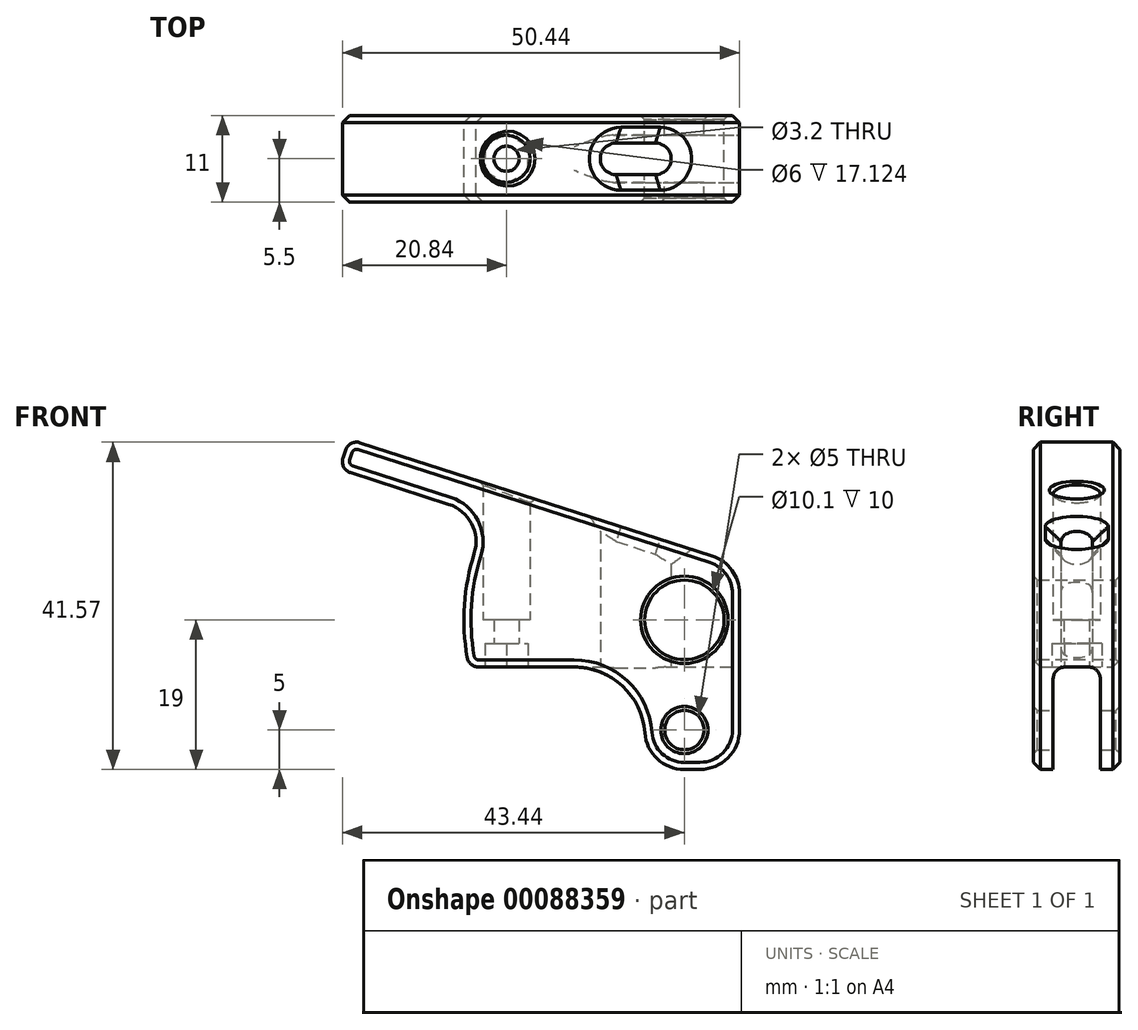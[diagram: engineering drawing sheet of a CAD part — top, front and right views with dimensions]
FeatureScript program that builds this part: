
annotation { "Feature Type Name" : "Feature", "Feature Type Description" : "" }
export const myFeature = defineFeature(function(context is Context, id is Id, definition is map)
    precondition{}
    {
        {
            var Q0;
            Q0=qCreatedBy(makeId("Front.planeOp"),FACE);
            var sketch = newSketch(context, id + "F0", { "sketchPlane" : qUnion([Q0])});
            skCircle(sketch, "E0", {"center": v(0, 0) * mm, "radius": 5.05 * mm});
            skCircle(sketch, "E1", {"center": v(0, -14) * mm, "radius": 2.5 * mm});
            skLineSegment(sketch, "E2.left", {"start": v(7, 7) * mm, "end": v(7, -19) * mm});
            skLineSegment(sketch, "E3.bottom", {"start": v(7, -19) * mm, "end": v(-5, -19) * mm});
            skLineSegment(sketch, "E3.right", {"start": v(-5, -19) * mm, "end": v(-5, -6) * mm});
            skLineSegment(sketch, "E4.trimOffspring", {"start": v(-5, -6) * mm, "end": v(-27.35, -6) * mm});
            skArc(sketch, "E5", {"start": v(-24.79, 13.02) * mm, "mid": v(-27.75, 3.74) * mm, "end": v(-27.35, -6) * mm});
            skLineSegment(sketch, "E6", {"start": v(-24.79, 13.02) * mm, "end": v(-43.83, 19.15) * mm});
            skLineSegment(sketch, "E7", {"start": v(-43.83, 19.15) * mm, "end": v(-42.6, 22.96) * mm});
            skLineSegment(sketch, "E8", {"start": v(-42.6, 22.96) * mm, "end": v(7, 7) * mm});
            skSolve(sketch);
        }
        {
            var Q0;
            Q0 = qSketchRegion(id + "F0", true);
            extrude(context, id + "F1", {"entities" : qUnion([Q0]), "endBound" : BoundingType.SYMMETRIC, "depth" : 11 * mm});
        }
        {
            var Q0;
            Q0=makeQuery(id+"F1.opExtrude","SWEPT_FACE",FACE,{"disambiguationData":[OSD([sQuery(id+"F0.wireOp",EDGE,"E3.bottom")])]});
            var sketch = newSketch(context, id + "F2", { "sketchPlane" : qUnion([Q0])});
            skLineSegment(sketch, "E9.bottom", {"start": v(7, 3) * mm, "end": v(-7, 3) * mm});
            skLineSegment(sketch, "E9.top", {"start": v(7, -3) * mm, "end": v(-7, -3) * mm});
            skLineSegment(sketch, "E9.left", {"start": v(7, 3) * mm, "end": v(7, -3) * mm});
            skLineSegment(sketch, "E9.right", {"start": v(-7, 3) * mm, "end": v(-7, -3) * mm});
            skPoint(sketch, "E9.middle", {"position": v(0, 0) * mm});
            skSolve(sketch);
        }
        {
            var Q0;
            Q0 = qSketchRegion(id + "F2", true);
            var Q1;
            Q1=makeQuery(id+"F1.opExtrude","SWEPT_FACE",FACE,{"disambiguationData":[OSD([sQuery(id+"F0.wireOp",EDGE,"E4.trimOffspring")])]});
            extrude(context, id + "F3", {"entities" : qUnion([Q0]), "operationType" : NewBodyOperationType.REMOVE, "endBound" : BoundingType.UP_TO_SURFACE, "oppositeDirection" : true, "endBoundEntityFace" : qUnion([Q1]), "depth" : 25 * mm});
        }
        {
            var Q0;
            Q0=makeQuery(id+"F3.boolean.opBoolean","MERGE",FACE,{"derivedFrom":[makeQuery(id+"F1.opExtrude","SWEPT_FACE",FACE,{"disambiguationData":[OSD([sQuery(id+"F0.wireOp",EDGE,"E4.trimOffspring")])]}),makeQuery(id+"F3.opExtrude","CAP_FACE",FACE,{"disambiguationData":[OSD([sQuery(id+"F2.wireOp",EDGE,"E9.bottom"),sQuery(id+"F2.wireOp",EDGE,"E9.top"),sQuery(id+"F2.wireOp",EDGE,"E9.left"),sQuery(id+"F2.wireOp",EDGE,"E9.right")])],"isStart":false})]});
            var sketch = newSketch(context, id + "F4", { "sketchPlane" : qUnion([Q0])});
            skLineSegment(sketch, "E10.bottom", {"start": v(-3.68, -2) * mm, "end": v(-8.68, -2) * mm});
            skLineSegment(sketch, "E10.top", {"start": v(-3.68, 2) * mm, "end": v(-8.68, 2) * mm});
            skPoint(sketch, "E10.middle", {"position": v(-6.18, 0) * mm});
            skArc(sketch, "E11", {"start": v(-8.68, 2) * mm, "mid": v(-10.68, 0) * mm, "end": v(-8.68, -2) * mm});
            skArc(sketch, "E12", {"start": v(-3.68, -2) * mm, "mid": v(-1.68, 0) * mm, "end": v(-3.68, 2) * mm});
            skSolve(sketch);
        }
        {
            var Q0;
            Q0 = qSketchRegion(id + "F4", true);
            extrude(context, id + "F5", {"entities" : qUnion([Q0]), "operationType" : NewBodyOperationType.REMOVE, "endBound" : BoundingType.THROUGH_ALL, "oppositeDirection" : true, "depth" : 25 * mm});
        }
        {
            var Q0;
            {var subQ0=sQuery(id+"F0.wireOp",EDGE,"E4.trimOffspring");var subQ2=sQuery(id+"F2.wireOp",EDGE,"E9.bottom");var subQ3=sQuery(id+"F0.wireOp",EDGE,"E3.right");Q0=makeQuery(id+"F3.boolean.opBoolean","SPLIT",EDGE,{"disambiguationData":[TD([makeQuery(id+"F3.opExtrude","SWEPT_FACE",FACE,{"disambiguationData":[OSD([subQ2])]})])],"derivedFrom":makeQuery(id+"F1.opExtrude","SWEPT_EDGE",EDGE,{"disambiguationData":[OSD([subQ3,subQ0])]})});}
            var Q1;
            {var subQ0=sQuery(id+"F0.wireOp",EDGE,"E4.trimOffspring");var subQ1=sQuery(id+"F0.wireOp",EDGE,"E3.right");var subQ3=sQuery(id+"F2.wireOp",EDGE,"E9.top");Q1=makeQuery(id+"F3.boolean.opBoolean","SPLIT",EDGE,{"disambiguationData":[TD([makeQuery(id+"F3.opExtrude","SWEPT_FACE",FACE,{"disambiguationData":[OSD([subQ3])]})])],"derivedFrom":makeQuery(id+"F1.opExtrude","SWEPT_EDGE",EDGE,{"disambiguationData":[OSD([subQ1,subQ0])]})});}
            fillet(context, id + "F6", {"entities" : qUnion([Q0, Q1]), "radius" : 9 * mm, "tangentPropagation" : true, "allowEdgeOverflow" : false});
        }
        {
            var Q0;
            {var subQ0=sQuery(id+"F0.wireOp",EDGE,"E3.right");var subQ1=sQuery(id+"F0.wireOp",EDGE,"E3.bottom");Q0=makeQuery(id+"F3.boolean.opBoolean","SPLIT",EDGE,{"disambiguationData":[TD([makeQuery(id+"F3.opExtrude","SWEPT_FACE",FACE,{"disambiguationData":[OSD([sQuery(id+"F2.wireOp",EDGE,"E9.bottom")])]})])],"derivedFrom":makeQuery(id+"F1.opExtrude","SWEPT_EDGE",EDGE,{"disambiguationData":[OSD([subQ1,subQ0])]})});}
            var Q1;
            {var subQ0=sQuery(id+"F0.wireOp",EDGE,"E3.right");var subQ1=sQuery(id+"F0.wireOp",EDGE,"E3.bottom");Q1=makeQuery(id+"F3.boolean.opBoolean","SPLIT",EDGE,{"disambiguationData":[TD([makeQuery(id+"F3.opExtrude","SWEPT_FACE",FACE,{"disambiguationData":[OSD([sQuery(id+"F2.wireOp",EDGE,"E9.top")])]})])],"derivedFrom":makeQuery(id+"F1.opExtrude","SWEPT_EDGE",EDGE,{"disambiguationData":[OSD([subQ1,subQ0])]})});}
            fillet(context, id + "F7", {"entities" : qUnion([Q0, Q1]), "radius" : 5 * mm, "tangentPropagation" : true, "allowEdgeOverflow" : false});
        }
        {
            var Q0;
            {var subQ0=sQuery(id+"F0.wireOp",EDGE,"E3.bottom");var subQ1=sQuery(id+"F0.wireOp",EDGE,"E2.left");Q0=makeQuery(id+"F3.boolean.opBoolean","SPLIT",EDGE,{"disambiguationData":[TD([makeQuery(id+"F3.opExtrude","SWEPT_FACE",FACE,{"disambiguationData":[OSD([sQuery(id+"F2.wireOp",EDGE,"E9.bottom")])]})])],"derivedFrom":makeQuery(id+"F1.opExtrude","SWEPT_EDGE",EDGE,{"disambiguationData":[OSD([subQ1,subQ0])]})});}
            var Q1;
            {var subQ0=sQuery(id+"F0.wireOp",EDGE,"E3.bottom");var subQ1=sQuery(id+"F0.wireOp",EDGE,"E2.left");Q1=makeQuery(id+"F3.boolean.opBoolean","SPLIT",EDGE,{"disambiguationData":[TD([makeQuery(id+"F3.opExtrude","SWEPT_FACE",FACE,{"disambiguationData":[OSD([sQuery(id+"F2.wireOp",EDGE,"E9.top")])]})])],"derivedFrom":makeQuery(id+"F1.opExtrude","SWEPT_EDGE",EDGE,{"disambiguationData":[OSD([subQ1,subQ0])]})});}
            fillet(context, id + "F8", {"entities" : qUnion([Q0, Q1]), "radius" : 5 * mm, "tangentPropagation" : true, "allowEdgeOverflow" : false});
        }
        {
            var Q0;
            Q0=makeQuery(id+"F3.boolean.opBoolean","COPY",EDGE,{"derivedFrom":makeQuery(id+"F3.opExtrude","CAP_EDGE",EDGE,{"disambiguationData":[OSD([sQuery(id+"F2.wireOp",EDGE,"E9.bottom")])],"isStart":false})});
            var Q1;
            Q1=makeQuery(id+"F3.boolean.opBoolean","COPY",EDGE,{"derivedFrom":makeQuery(id+"F3.opExtrude","CAP_EDGE",EDGE,{"disambiguationData":[OSD([sQuery(id+"F2.wireOp",EDGE,"E9.top")])],"isStart":false})});
            fillet(context, id + "F9", {"entities" : qUnion([Q0, Q1]), "radius" : 1.5 * mm, "tangentPropagation" : true, "allowEdgeOverflow" : false});
        }
        {
            var Q0;
            Q0=makeQuery(id+"F1.opExtrude","SWEPT_EDGE",EDGE,{"disambiguationData":[OSD([sQuery(id+"F0.wireOp",EDGE,"E5"),sQuery(id+"F0.wireOp",EDGE,"E6")])]});
            fillet(context, id + "F10", {"entities" : qUnion([Q0]), "radius" : 5 * mm, "tangentPropagation" : true, "allowEdgeOverflow" : false});
        }
        {
            var Q0;
            Q0=makeQuery(id+"F1.opExtrude","SWEPT_EDGE",EDGE,{"disambiguationData":[OSD([sQuery(id+"F0.wireOp",EDGE,"E2.bottom"),sQuery(id+"F0.wireOp",EDGE,"E2.left")])]});
            fillet(context, id + "F11", {"entities" : qUnion([Q0]), "radius" : 5 * mm, "tangentPropagation" : true, "allowEdgeOverflow" : false});
        }
        {
            var Q0;
            Q0=makeQuery(id+"F9.opFillet","SPLIT",FACE,{"disambiguationData":[OD(0.0)],"derivedFrom":makeQuery(id+"F3.boolean.opBoolean","MERGE",FACE,{"derivedFrom":[makeQuery(id+"F1.opExtrude","SWEPT_FACE",FACE,{"disambiguationData":[OSD([sQuery(id+"F0.wireOp",EDGE,"E4.trimOffspring")])]}),makeQuery(id+"F3.opExtrude","CAP_FACE",FACE,{"disambiguationData":[OSD([sQuery(id+"F2.wireOp",EDGE,"E9.bottom"),sQuery(id+"F2.wireOp",EDGE,"E9.top"),sQuery(id+"F2.wireOp",EDGE,"E9.left"),sQuery(id+"F2.wireOp",EDGE,"E9.right")])],"isStart":false})]})});
            var sketch = newSketch(context, id + "F12", { "sketchPlane" : qUnion([Q0])});
            skCircle(sketch, "E13.cCircle", {"center": v(-22.6, 0) * mm, "radius": 2.75 * mm, "construction": true});
            skLineSegment(sketch, "E13.0", {"start": v(-19.85, 1.59) * mm, "end": v(-19.85, -1.59) * mm});
            skLineSegment(sketch, "E13.1", {"start": v(-19.85, -1.59) * mm, "end": v(-22.6, -3.18) * mm});
            skLineSegment(sketch, "E13.2", {"start": v(-22.6, -3.18) * mm, "end": v(-25.35, -1.59) * mm});
            skLineSegment(sketch, "E13.3", {"start": v(-25.35, -1.59) * mm, "end": v(-25.35, 1.59) * mm});
            skLineSegment(sketch, "E13.4", {"start": v(-25.35, 1.59) * mm, "end": v(-22.6, 3.18) * mm});
            skLineSegment(sketch, "E13.5", {"start": v(-22.6, 3.18) * mm, "end": v(-19.85, 1.59) * mm});
            skPoint(sketch, "E13.0.midPoint", {"position": v(-19.85, 0) * mm});
            skSolve(sketch);
        }
        {
            var Q0;
            Q0 = qSketchRegion(id + "F12", true);
            extrude(context, id + "F13", {"entities" : qUnion([Q0]), "operationType" : NewBodyOperationType.REMOVE, "oppositeDirection" : true, "depth" : 3 * mm});
        }
        {
            var Q0;
            Q0=makeQuery(id+"F13.boolean.opBoolean","COPY",FACE,{"derivedFrom":makeQuery(id+"F13.opExtrude","CAP_FACE",FACE,{"disambiguationData":[OSD([sQuery(id+"F12.wireOp",EDGE,"E13.0"),sQuery(id+"F12.wireOp",EDGE,"E13.1"),sQuery(id+"F12.wireOp",EDGE,"E13.2"),sQuery(id+"F12.wireOp",EDGE,"E13.3"),sQuery(id+"F12.wireOp",EDGE,"E13.4"),sQuery(id+"F12.wireOp",EDGE,"E13.5")])],"isStart":false})});
            var sketch = newSketch(context, id + "F14", { "sketchPlane" : qUnion([Q0])});
            skCircle(sketch, "E14", {"center": v(-22.6, 0) * mm, "radius": 1.6 * mm});
            skLineSegment(sketch, "E15", {"start": v(-25.35, 0) * mm, "end": v(-19.85, 0) * mm, "construction": true});
            skSolve(sketch);
        }
        {
            var Q0;
            Q0 = qSketchRegion(id + "F14", true);
            extrude(context, id + "F15", {"entities" : qUnion([Q0]), "operationType" : NewBodyOperationType.REMOVE, "endBound" : BoundingType.THROUGH_ALL, "oppositeDirection" : true, "depth" : 25 * mm});
        }
        {
            var Q0;
            Q0=qCreatedBy(makeId("Top.planeOp"),FACE);
            var sketch = newSketch(context, id + "F16", { "sketchPlane" : qUnion([Q0])});
            skCircle(sketch, "E16", {"center": v(-22.6, 0) * mm, "radius": 3 * mm});
            skSolve(sketch);
        }
        {
            var Q0;
            Q0 = qSketchRegion(id + "F16", true);
            extrude(context, id + "F17", {"entities" : qUnion([Q0]), "operationType" : NewBodyOperationType.REMOVE, "endBound" : BoundingType.THROUGH_ALL, "depth" : 25 * mm});
        }
        {
            var Q0;
            Q0=makeQuery(id+"F1.opExtrude","SWEPT_EDGE",EDGE,{"disambiguationData":[OSD([sQuery(id+"F0.wireOp",EDGE,"E4.trimOffspring"),sQuery(id+"F0.wireOp",EDGE,"E5")])]});
            var Q1;
            Q1=makeQuery(id+"F1.opExtrude","SWEPT_EDGE",EDGE,{"disambiguationData":[OSD([sQuery(id+"F0.wireOp",EDGE,"E6"),sQuery(id+"F0.wireOp",EDGE,"E7")])]});
            var Q2;
            Q2=makeQuery(id+"F1.opExtrude","SWEPT_EDGE",EDGE,{"disambiguationData":[OSD([sQuery(id+"F0.wireOp",EDGE,"E7"),sQuery(id+"F0.wireOp",EDGE,"E8")])]});
            fillet(context, id + "F18", {"entities" : qUnion([Q0, Q1, Q2]), "radius" : 1.5 * mm, "tangentPropagation" : true, "allowEdgeOverflow" : false});
        }
        {
            var Q0;
            Q0=makeQuery(id+"F1.opExtrude","CAP_EDGE",EDGE,{"disambiguationData":[OSD([sQuery(id+"F0.wireOp",EDGE,"E8")])],"isStart":true});
            var Q1;
            Q1=makeQuery(id+"F1.opExtrude","CAP_EDGE",EDGE,{"disambiguationData":[OSD([sQuery(id+"F0.wireOp",EDGE,"E4.trimOffspring")])],"isStart":false});
            chamfer(context, id + "F19", {"entities" : qUnion([Q0, Q1]), "width" : .9 * mm, "tangentPropagation" : true});
        }
        {
            var Q0;
            Q0=makeQuery(id+"F17.boolean.opBoolean","INTERSECT",EDGE,{"derivedFrom":[makeQuery(id+"F1.opExtrude","SWEPT_FACE",FACE,{"disambiguationData":[OSD([sQuery(id+"F0.wireOp",EDGE,"E8")])]}),makeQuery(id+"F17.opExtrude","SWEPT_FACE",FACE,{"disambiguationData":[OSD([sQuery(id+"F16.wireOp",EDGE,"E16")])]})]});
            var Q1;
            Q1=makeQuery(id+"F1.opExtrude","CAP_EDGE",EDGE,{"disambiguationData":[OSD([sQuery(id+"F0.wireOp",EDGE,"E0")])],"isStart":false});
            var Q2;
            Q2=makeQuery(id+"F1.opExtrude","CAP_EDGE",EDGE,{"disambiguationData":[OSD([sQuery(id+"F0.wireOp",EDGE,"E1")])],"isStart":false});
            var Q3;
            Q3=makeQuery(id+"F1.opExtrude","CAP_EDGE",EDGE,{"disambiguationData":[OSD([sQuery(id+"F0.wireOp",EDGE,"E0")])],"isStart":true});
            var Q4;
            Q4=makeQuery(id+"F1.opExtrude","CAP_EDGE",EDGE,{"disambiguationData":[OSD([sQuery(id+"F0.wireOp",EDGE,"E1")])],"isStart":true});
            var Q5;
            Q5=makeQuery(id+"F5.boolean.opBoolean","COPY",EDGE,{"derivedFrom":makeQuery(id+"F5.opExtrude","CAP_EDGE",EDGE,{"disambiguationData":[OSD([sQuery(id+"F4.wireOp",EDGE,"E11")])],"isStart":true})});
            var Q6;
            Q6=makeQuery(id+"F15.boolean.opBoolean","COPY",EDGE,{"derivedFrom":makeQuery(id+"F15.opExtrude","CAP_EDGE",EDGE,{"disambiguationData":[OSD([sQuery(id+"F14.wireOp",EDGE,"E14")])],"isStart":true})});
            var Q7;
            Q7=makeQuery(id+"F13.boolean.opBoolean","COPY",EDGE,{"derivedFrom":makeQuery(id+"F13.opExtrude","CAP_EDGE",EDGE,{"disambiguationData":[OSD([sQuery(id+"F12.wireOp",EDGE,"E13.5")])],"isStart":true})});
            var Q8;
            Q8=makeQuery(id+"F13.boolean.opBoolean","COPY",EDGE,{"derivedFrom":makeQuery(id+"F13.opExtrude","CAP_EDGE",EDGE,{"disambiguationData":[OSD([sQuery(id+"F12.wireOp",EDGE,"E13.0")])],"isStart":true})});
            var Q9;
            Q9=makeQuery(id+"F13.boolean.opBoolean","COPY",EDGE,{"derivedFrom":makeQuery(id+"F13.opExtrude","CAP_EDGE",EDGE,{"disambiguationData":[OSD([sQuery(id+"F12.wireOp",EDGE,"E13.1")])],"isStart":true})});
            var Q10;
            Q10=makeQuery(id+"F13.boolean.opBoolean","COPY",EDGE,{"derivedFrom":makeQuery(id+"F13.opExtrude","CAP_EDGE",EDGE,{"disambiguationData":[OSD([sQuery(id+"F12.wireOp",EDGE,"E13.2")])],"isStart":true})});
            var Q11;
            Q11=makeQuery(id+"F13.boolean.opBoolean","COPY",EDGE,{"derivedFrom":makeQuery(id+"F13.opExtrude","CAP_EDGE",EDGE,{"disambiguationData":[OSD([sQuery(id+"F12.wireOp",EDGE,"E13.3")])],"isStart":true})});
            var Q12;
            Q12=makeQuery(id+"F13.boolean.opBoolean","COPY",EDGE,{"derivedFrom":makeQuery(id+"F13.opExtrude","CAP_EDGE",EDGE,{"disambiguationData":[OSD([sQuery(id+"F12.wireOp",EDGE,"E13.4")])],"isStart":true})});
            chamfer(context, id + "F20", {"entities" : qUnion([Q0, Q1, Q2, Q3, Q4, Q5, Q6, Q7, Q8, Q9, Q10, Q11, Q12]), "width" : .5 * mm, "tangentPropagation" : true});
        }
        {
            var Q0;
            Q0=makeQuery(id+"F5.boolean.opBoolean","INTERSECT",EDGE,{"derivedFrom":[makeQuery(id+"F1.opExtrude","SWEPT_FACE",FACE,{"disambiguationData":[OSD([sQuery(id+"F0.wireOp",EDGE,"E8")])]}),makeQuery(id+"F5.opExtrude","SWEPT_FACE",FACE,{"disambiguationData":[OSD([sQuery(id+"F4.wireOp",EDGE,"E10.bottom")])]})]});
            chamfer(context, id + "F21", {"entities" : qUnion([Q0]), "width" : 2 * mm, "tangentPropagation" : true});
        }
    });
